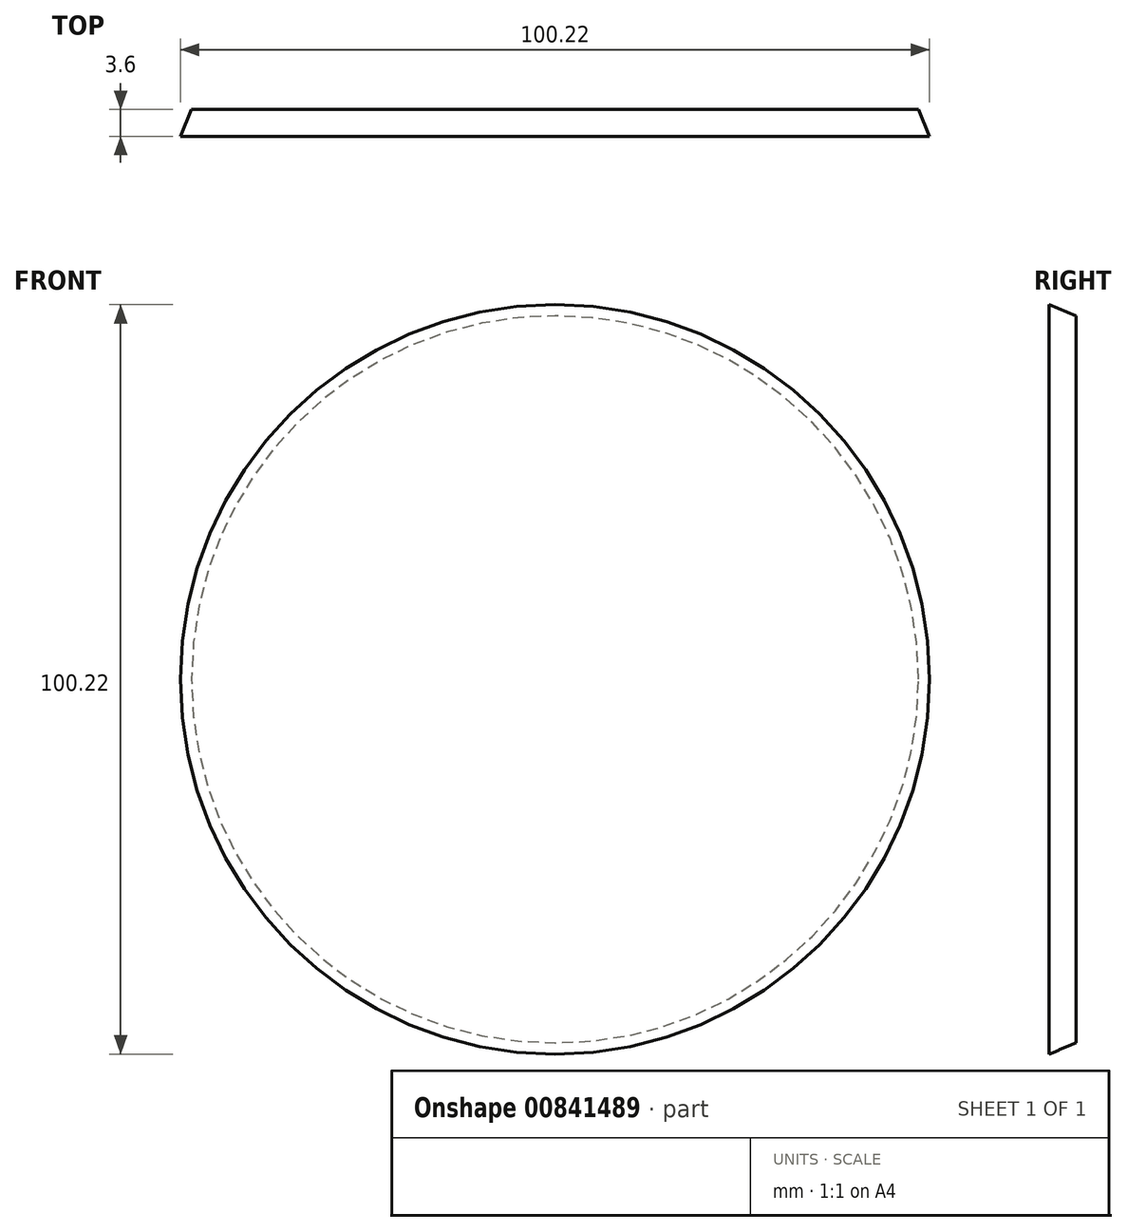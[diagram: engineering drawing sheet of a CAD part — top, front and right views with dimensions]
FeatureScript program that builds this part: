
annotation { "Feature Type Name" : "Feature", "Feature Type Description" : "" }
export const myFeature = defineFeature(function(context is Context, id is Id, definition is map)
    precondition{}
    {
        {
            var Q0;
            Q0=qCreatedBy(makeId("Front.planeOp"),FACE);
            var sketch = newSketch(context, id + "F0", { "sketchPlane" : qUnion([Q0])});
            skCircle(sketch, "E0", {"center": v(-8.04, 1.05) * mm, "radius": 62.37 * mm});
            skPoint(sketch, "E0.first.point", {"position": v(36.15, 45.07) * mm});
            skPoint(sketch, "E0.second.point", {"position": v(-56.48, -38.24) * mm});
            skPoint(sketch, "E0.third.point", {"position": v(40.04, -38.68) * mm});
            skSolve(sketch);
        }
        {
            var Q0;
            Q0=makeQuery(id+"F0.imprint","IMPRINT",FACE,{"disambiguationData":[TD([[makeQuery(id+"F0.imprint","IMPRINT",EDGE,{"derivedFrom":sQuery(id+"F0.wireOp",EDGE,"E0")}),1.0]])]});
            extrude(context, id + "F1", {"entities" : qUnion([Q0]), "oppositeDirection" : true, "depth" : 3.6 * mm, "offsetDistance" : 25.4 * mm});
        }
        {
            var Q0;
            Q0=makeQuery(id+"F1.opExtrude","CAP_FACE",FACE,{"disambiguationData":[OSD([sQuery(id+"F0.wireOp",EDGE,"E0")])],"isStart":true});
            chamfer(context, id + "F2", {"entities" : qUnion([Q0]), "width" : 5.08 * mm, "tangentPropagation" : true});
        }
        {
            var Q0;
            Q0=makeQuery(id+"F1.opExtrude","CAP_FACE",FACE,{"disambiguationData":[OSD([sQuery(id+"F0.wireOp",EDGE,"E0")])],"isStart":false});
            chamfer(context, id + "F3", {"entities" : qUnion([Q0]), "width" : 5.08 * mm, "tangentPropagation" : true});
        }
    });
